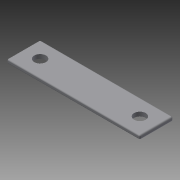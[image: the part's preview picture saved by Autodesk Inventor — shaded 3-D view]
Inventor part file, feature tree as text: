
AUTODESK INVENTOR PART (.ipt)
format: ipt  version: 2014 SP1 (Build 180222100, 222)  size: 103,424 bytes
history: native  units: in
note: dims shown in document units (in); Inventor stores cm internally (conversion verified against a paired STEP export)
features: extrude x2, sketch x2, fillet x1
ambient origin geometry x8: Origin, YZ Plane, XZ Plane, XY Plane, X Axis, Y Axis, Z Axis, Center Point
bodies: Solid1 (feature_tree)
feature tree (5):
  extrude  "Extrusion1"  Depth=0.5in
  extrude  "Extrusion2"  Depth=0.02in
  fillet  "Fillet1"  Radius=0.25in
  sketch  "Sketch1"  dims[d0=2.0in d1=0.5in]
  sketch  "Sketch2"  dims[d2=0.0625in d3=0.0in d4=0.175in d5=0.25in d6=0.175in d7=0.25in d8=0.25in d9=0.25in d10=0.0625in d11=0.0in d12=0.02in]
